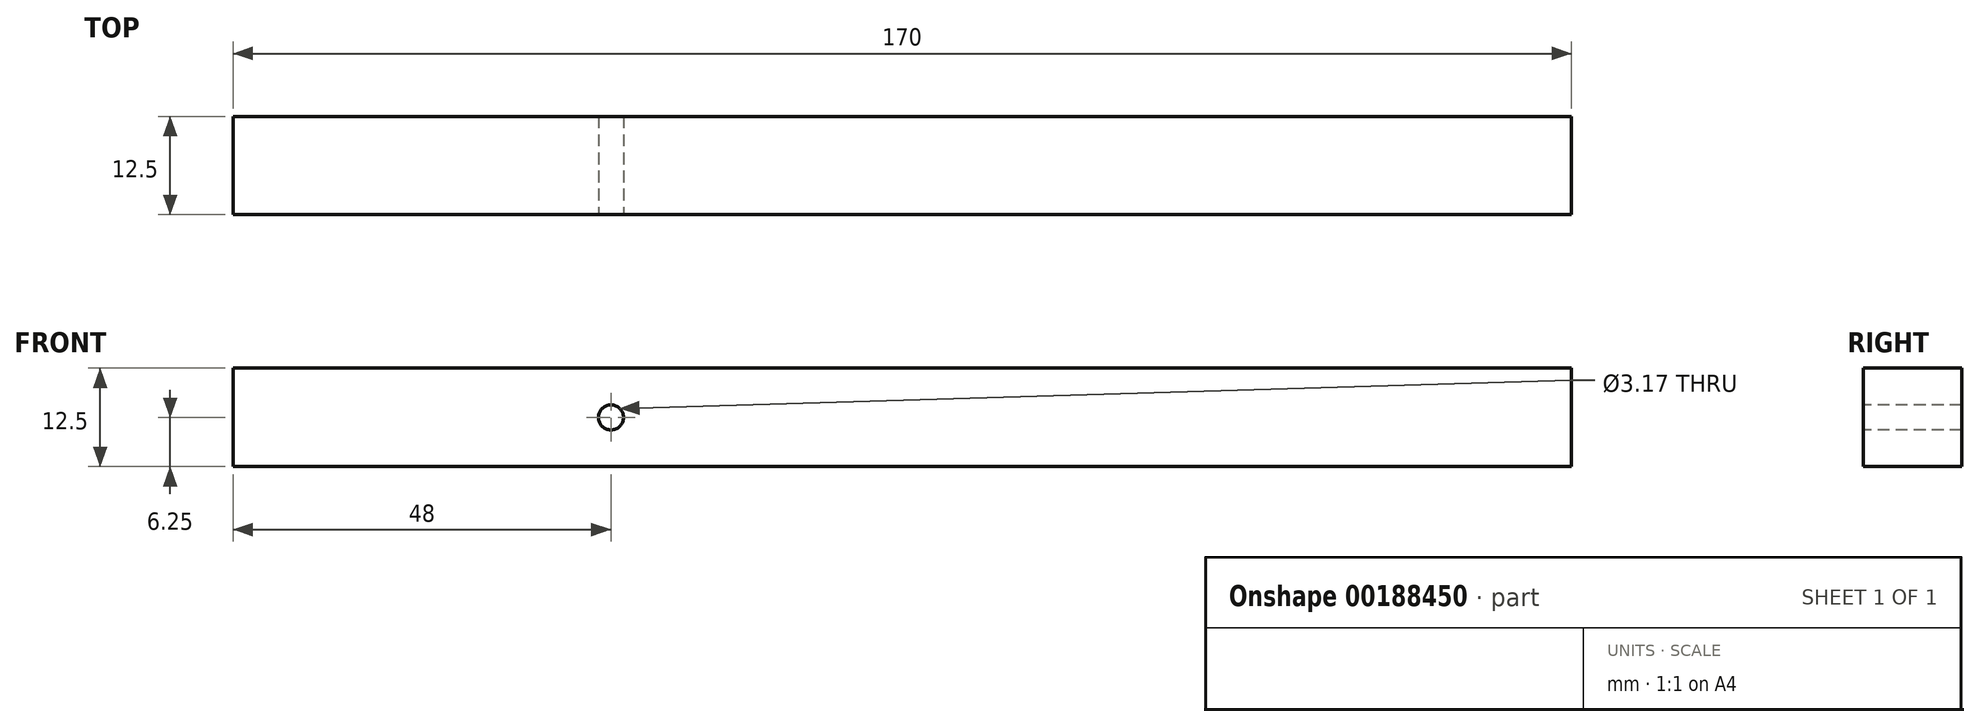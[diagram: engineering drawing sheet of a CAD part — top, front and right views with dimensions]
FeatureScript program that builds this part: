
annotation { "Feature Type Name" : "Feature", "Feature Type Description" : "" }
export const myFeature = defineFeature(function(context is Context, id is Id, definition is map)
    precondition{}
    {
        {
            var Q0;
            Q0=qCreatedBy(makeId("Right.planeOp"),FACE);
            var sketch = newSketch(context, id + "F0", { "sketchPlane" : qUnion([Q0])});
            skLineSegment(sketch, "E0.bottom", {"start": v(-6.25, 6.25) * mm, "end": v(6.25, 6.25) * mm});
            skLineSegment(sketch, "E0.top", {"start": v(-6.25, -6.25) * mm, "end": v(6.25, -6.25) * mm});
            skLineSegment(sketch, "E0.left", {"start": v(-6.25, 6.25) * mm, "end": v(-6.25, -6.25) * mm});
            skLineSegment(sketch, "E0.right", {"start": v(6.25, 6.25) * mm, "end": v(6.25, -6.25) * mm});
            skPoint(sketch, "E0.middle", {"position": v(0, 0) * mm});
            skSolve(sketch);
        }
        {
            var Q0;
            Q0 = qSketchRegion(id + "F0", true);
            extrude(context, id + "F1", {"entities" : qUnion([Q0]), "depth" : 170 * mm, "offsetDistance" : 25 * mm});
        }
        {
            var Q0;
            Q0=makeQuery(id+"F1.opExtrude","SWEPT_FACE",FACE,{"disambiguationData":[OSD([sQuery(id+"F0.wireOp",EDGE,"E0.left")])]});
            var sketch = newSketch(context, id + "F2", { "sketchPlane" : qUnion([Q0])});
            skPoint(sketch, "E1", {"position": v(48, 0) * mm});
            skSolve(sketch);
        }
        {
            var Q0;
            Q0=sQuery(id+"F2.wireOp",VERTEX,"E1");
            var Q1;
            Q1=makeQuery(id+"F1.opExtrude","SWEPT_BODY",BODY,{"disambiguationData":[OSD([sQuery(id+"F0.wireOp",EDGE,"E0.bottom"),sQuery(id+"F0.wireOp",EDGE,"E0.top"),sQuery(id+"F0.wireOp",EDGE,"E0.left"),sQuery(id+"F0.wireOp",EDGE,"E0.right")])]});
            hole(context, id + "F3", {"style" : HoleStyle.SIMPLE, "endStyle" : HoleEndStyle.THROUGH, "holeDiameter" : 3.17 * mm, "majorDiameter" : 5 * mm, "isTappedThrough" : true, "tappedDepth" : 12 * mm, "tapClearance" : 3, "startFromSketch" : true, "locations" : qUnion([Q0]), "scope" : qUnion([Q1])});
        }
    });
